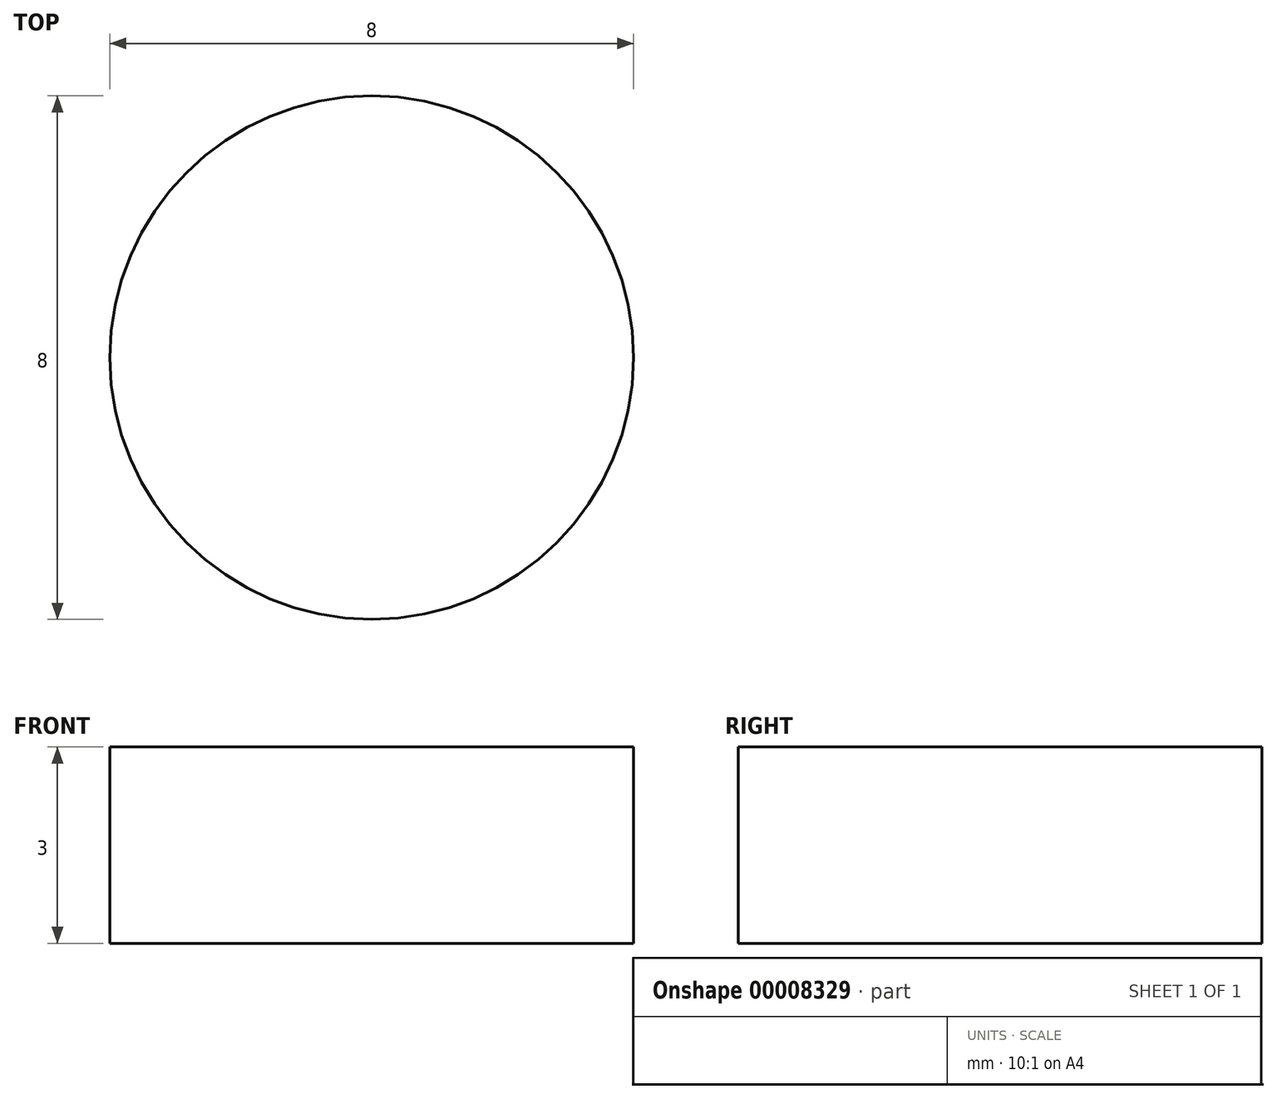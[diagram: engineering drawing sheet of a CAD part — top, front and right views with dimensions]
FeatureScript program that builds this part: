
annotation { "Feature Type Name" : "Feature", "Feature Type Description" : "" }
export const myFeature = defineFeature(function(context is Context, id is Id, definition is map)
    precondition{}
    {
        {
            var Q0;
            Q0=qCreatedBy(makeId("Top.planeOp"),FACE);
            var sketch = newSketch(context, id + "F0", { "sketchPlane" : qUnion([Q0])});
            skLineSegment(sketch, "E0.bottom", {"start": v(0, 0) * mm, "end": v(25, 0) * mm});
            skLineSegment(sketch, "E0.top", {"start": v(0, 12.5) * mm, "end": v(25, 12.5) * mm});
            skLineSegment(sketch, "E0.left", {"start": v(0, 0) * mm, "end": v(0, 12.5) * mm});
            skLineSegment(sketch, "E0.right", {"start": v(25, 0) * mm, "end": v(25, 12.5) * mm});
            skLineSegment(sketch, "E1.0.MirrorCS", {"start": v(25, 0) * mm, "end": v(25, -12.5) * mm});
            skLineSegment(sketch, "E1.1.MirrorCS", {"start": v(0, -12.5) * mm, "end": v(25, -12.5) * mm});
            skLineSegment(sketch, "E1.3.MirrorCS", {"start": v(0, 0) * mm, "end": v(0, -12.5) * mm});
            skArc(sketch, "E2", {"start": v(25, -12.5) * mm, "mid": v(37.5, 0) * mm, "end": v(25, 12.5) * mm});
            skLineSegment(sketch, "E3.0.MirrorCS", {"start": v(0, 0) * mm, "end": v(-25, 0) * mm});
            skArc(sketch, "E3.2.MirrorCS", {"start": v(-25, -12.5) * mm, "mid": v(-37.5, 0) * mm, "end": v(-25, 12.5) * mm});
            skLineSegment(sketch, "E3.3.MirrorCS", {"start": v(0, 0) * mm, "end": v(-25, 0) * mm});
            skLineSegment(sketch, "E3.5.MirrorCS", {"start": v(0, -12.5) * mm, "end": v(-25, -12.5) * mm});
            skLineSegment(sketch, "E3.6.MirrorCS", {"start": v(-25, 0) * mm, "end": v(-25, 12.5) * mm});
            skLineSegment(sketch, "E3.7.MirrorCS", {"start": v(0, 12.5) * mm, "end": v(-25, 12.5) * mm});
            skLineSegment(sketch, "E3.8.MirrorCS", {"start": v(-25, 0) * mm, "end": v(-25, -12.5) * mm});
            skSolve(sketch);
        }
        {
            var Q0;
            Q0=makeQuery(id+"F0.imprint","IMPRINT",FACE,{"disambiguationData":[TD([[makeQuery(id+"F0.imprint","IMPRINT",EDGE,{"derivedFrom":sQuery(id+"F0.wireOp",EDGE,"E3.3.MirrorCS")}),-1.0]])]});
            var Q1;
            Q1=makeQuery(id+"F0.imprint","IMPRINT",FACE,{"disambiguationData":[TD([[makeQuery(id+"F0.imprint","IMPRINT",EDGE,{"derivedFrom":sQuery(id+"F0.wireOp",EDGE,"E1.0.MirrorCS")}),-1.0]])]});
            var Q2;
            Q2=makeQuery(id+"F0.imprint","IMPRINT",FACE,{"disambiguationData":[TD([[makeQuery(id+"F0.imprint","IMPRINT",EDGE,{"derivedFrom":sQuery(id+"F0.wireOp",EDGE,"E1.3.MirrorCS")}),-1.0]])]});
            var Q3;
            Q3=makeQuery(id+"F0.imprint","IMPRINT",FACE,{"disambiguationData":[TD([[makeQuery(id+"F0.imprint","IMPRINT",EDGE,{"derivedFrom":sQuery(id+"F0.wireOp",EDGE,"E3.2.MirrorCS")}),-1.0]])]});
            var Q4;
            Q4=makeQuery(id+"F0.imprint","IMPRINT",FACE,{"disambiguationData":[TD([[makeQuery(id+"F0.imprint","IMPRINT",EDGE,{"derivedFrom":sQuery(id+"F0.wireOp",EDGE,"E0.top")}),-1.0]])]});
            var Q5;
            Q5=makeQuery(id+"F0.imprint","IMPRINT",FACE,{"disambiguationData":[TD([[makeQuery(id+"F0.imprint","IMPRINT",EDGE,{"derivedFrom":sQuery(id+"F0.wireOp",EDGE,"E0.right")}),-1.0]])]});
            extrude(context, id + "F1", {"entities" : qUnion([Q0, Q1, Q2, Q3, Q4, Q5]), "depth" : 3 * mm});
        }
        {
            var Q0;
            Q0=makeQuery(id+"F1.opExtrude","CAP_FACE",FACE,{"disambiguationData":[OSD([sQuery(id+"F0.wireOp",EDGE,"E0.top"),sQuery(id+"F0.wireOp",EDGE,"E1.1.MirrorCS"),sQuery(id+"F0.wireOp",EDGE,"E2"),sQuery(id+"F0.wireOp",EDGE,"E3.2.MirrorCS"),sQuery(id+"F0.wireOp",EDGE,"E3.5.MirrorCS"),sQuery(id+"F0.wireOp",EDGE,"E3.7.MirrorCS")])],"isStart":true});
            var sketch = newSketch(context, id + "F2", { "sketchPlane" : qUnion([Q0])});
            skCircle(sketch, "E4", {"center": v(-25, 0) * mm, "radius": 4 * mm});
            skCircle(sketch, "E5.0.MirrorC", {"center": v(25, 0) * mm, "radius": 4 * mm});
            skLineSegment(sketch, "E6", {"start": v(0, -31.35) * mm, "end": v(0, 0) * mm, "construction": true});
            skSolve(sketch);
        }
        {
            var Q0;
            Q0=makeQuery(id+"F2.imprint","IMPRINT",FACE,{"disambiguationData":[TD([[makeQuery(id+"F2.imprint","IMPRINT",EDGE,{"derivedFrom":sQuery(id+"F2.wireOp",EDGE,"E4")}),1.0]])]});
            var Q1;
            Q1=makeQuery(id+"F2.imprint","IMPRINT",FACE,{"disambiguationData":[TD([[makeQuery(id+"F2.imprint","IMPRINT",EDGE,{"derivedFrom":sQuery(id+"F2.wireOp",EDGE,"E5.0.MirrorC")}),-1.0]])]});
            extrude(context, id + "F3", {"entities" : qUnion([Q0, Q1]), "operationType" : NewBodyOperationType.REMOVE, "endBound" : BoundingType.THROUGH_ALL, "oppositeDirection" : true, "depth" : 25 * mm});
        }
    });
